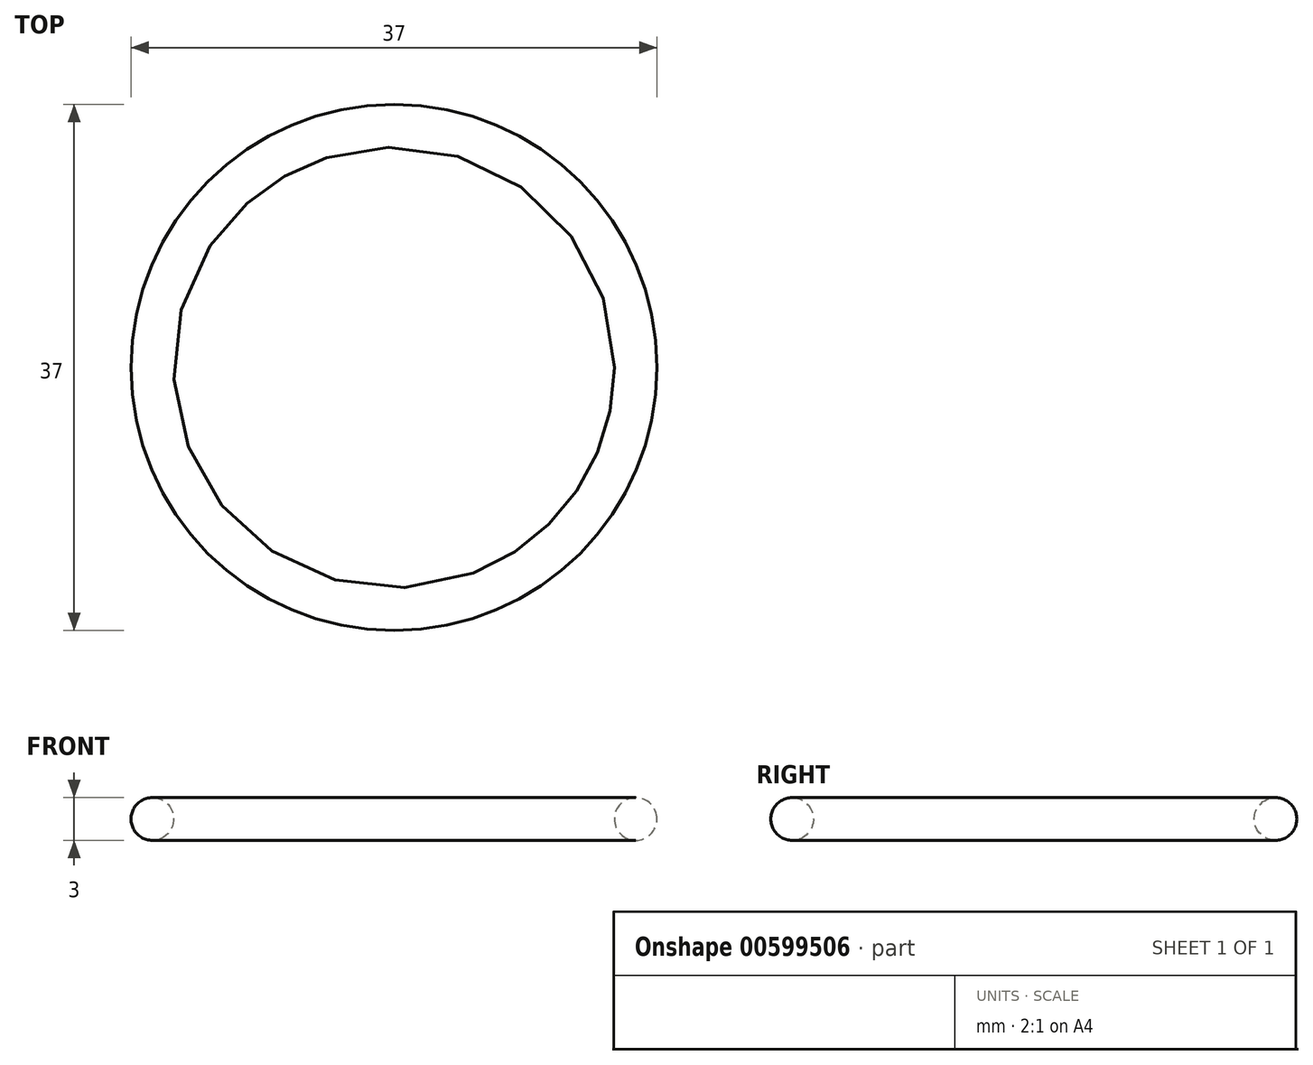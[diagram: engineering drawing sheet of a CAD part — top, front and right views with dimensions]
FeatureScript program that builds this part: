
annotation { "Feature Type Name" : "Feature", "Feature Type Description" : "" }
export const myFeature = defineFeature(function(context is Context, id is Id, definition is map)
    precondition{}
    {
        {
            var Q0;
            Q0=qCreatedBy(makeId("Front.planeOp"),FACE);
            var sketch = newSketch(context, id + "F0", { "sketchPlane" : qUnion([Q0])});
            skLineSegment(sketch, "E0", {"start": v(0, 7.14) * mm, "end": v(0, 0) * mm, "construction": true});
            skLineSegment(sketch, "E1", {"start": v(0, 0) * mm, "end": v(-17, 0) * mm, "construction": true});
            skCircle(sketch, "E2", {"center": v(-17, 0) * mm, "radius": 1.5 * mm});
            skSolve(sketch);
        }
        {
            var Q0;
            Q0 = qSketchRegion(id + "F0", true);
            var Q1;
            Q1=sQuery(id+"F0.wireOp",EDGE,"E0");
            revolve(context, id + "F1", {"entities" : qUnion([Q0]), "axis" : qUnion([Q1]), "revolveType" : RevolveType.FULL});
        }
    });
